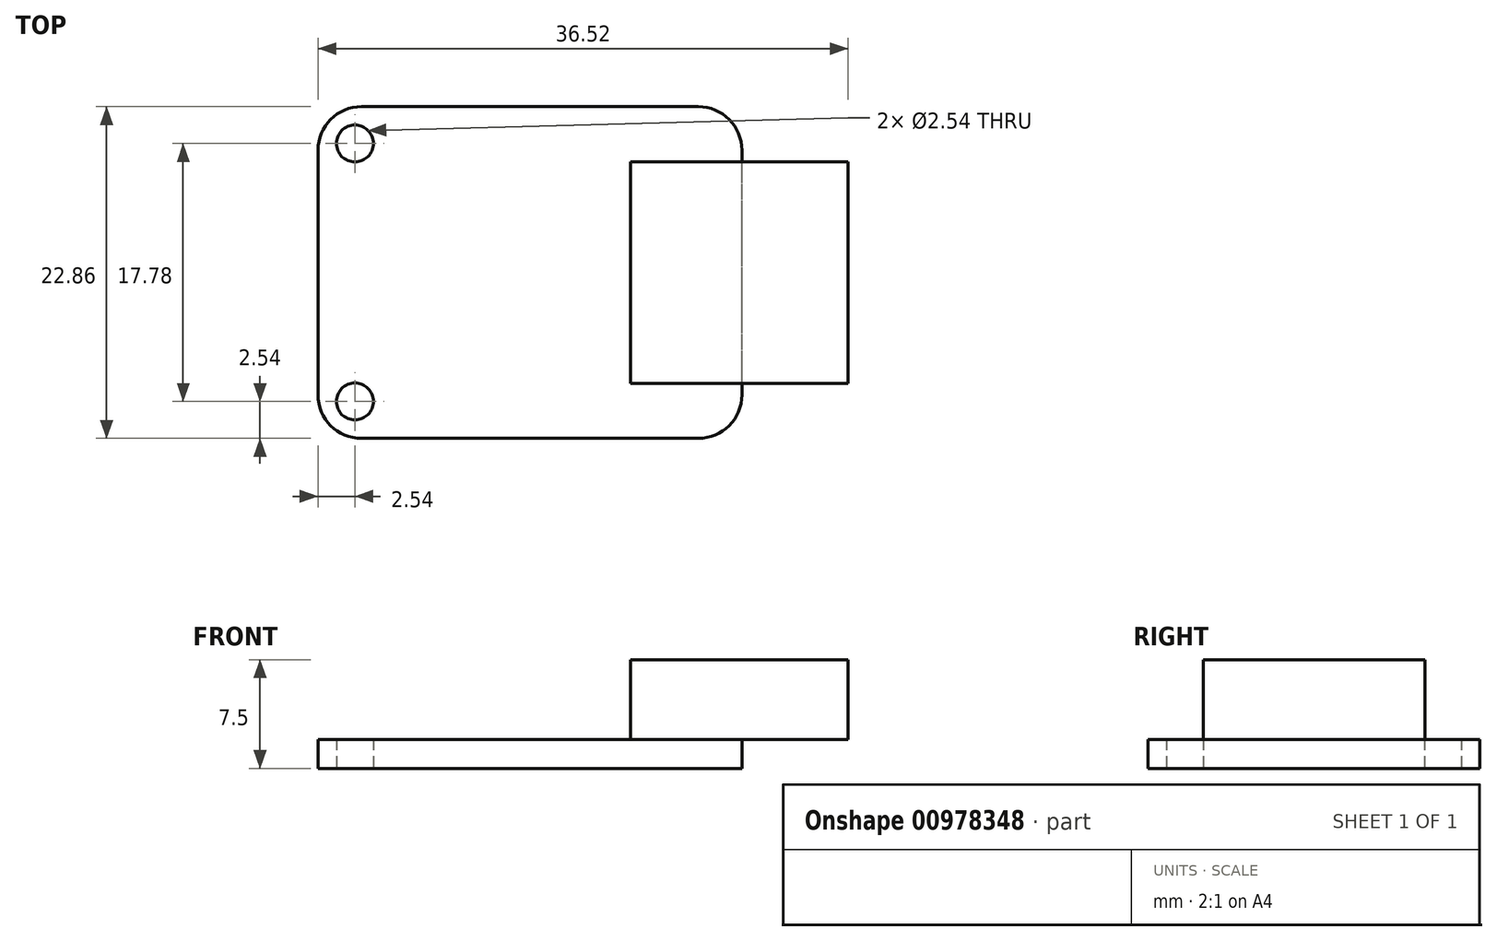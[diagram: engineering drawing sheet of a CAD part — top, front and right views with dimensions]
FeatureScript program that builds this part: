
annotation { "Feature Type Name" : "Feature", "Feature Type Description" : "" }
export const myFeature = defineFeature(function(context is Context, id is Id, definition is map)
    precondition{}
    {
        {
            var Q0;
            Q0=qCreatedBy(makeId("Top.planeOp"),FACE);
            var sketch = newSketch(context, id + "F0", { "sketchPlane" : qUnion([Q0])});
            skLineSegment(sketch, "E0.bottom", {"start": v(3, 0) * mm, "end": v(26.21, 0) * mm});
            skLineSegment(sketch, "E0.top", {"start": v(3, 22.86) * mm, "end": v(26.21, 22.86) * mm});
            skLineSegment(sketch, "E0.left", {"start": v(0, 3) * mm, "end": v(0, 19.86) * mm});
            skLineSegment(sketch, "E0.right", {"start": v(29.2, 3) * mm, "end": v(29.2, 19.86) * mm});
            skCircle(sketch, "E1", {"center": v(2.54, 2.54) * mm, "radius": 1.27 * mm});
            skCircle(sketch, "E2", {"center": v(2.54, 20.32) * mm, "radius": 1.27 * mm});
            skLineSegment(sketch, "E3", {"start": v(2.54, 2.54) * mm, "end": v(2.54, 0) * mm});
            skLineSegment(sketch, "E4", {"start": v(2.54, 2.54) * mm, "end": v(0, 2.54) * mm});
            skLineSegment(sketch, "E5", {"start": v(2.54, 20.32) * mm, "end": v(2.54, 22.86) * mm});
            skLineSegment(sketch, "E6", {"start": v(2.54, 20.32) * mm, "end": v(0, 20.32) * mm});
            skPoint(sketch, "E7.visualSharp", {"position": v(0, 22.86) * mm});
            skArc(sketch, "E7.filletArc", {"start": v(3, 22.86) * mm, "mid": v(0.88, 21.98) * mm, "end": v(0, 19.86) * mm});
            skPoint(sketch, "E8.visualSharp", {"position": v(0, 0) * mm});
            skArc(sketch, "E8.filletArc", {"start": v(0, 3) * mm, "mid": v(0.88, 0.88) * mm, "end": v(3, 0) * mm});
            skPoint(sketch, "E9.visualSharp", {"position": v(29.2, 22.86) * mm});
            skArc(sketch, "E9.filletArc", {"start": v(29.21, 19.86) * mm, "mid": v(28.33, 21.98) * mm, "end": v(26.21, 22.86) * mm});
            skPoint(sketch, "E10.visualSharp", {"position": v(29.2, 0) * mm});
            skArc(sketch, "E10.filletArc", {"start": v(26.21, 0) * mm, "mid": v(28.33, 0.88) * mm, "end": v(29.21, 3) * mm});
            skSolve(sketch);
        }
        {
            var Q0;
            {var subQ15=sQuery(id+"F0.wireOp",EDGE,"E0.bottom");Q0=makeQuery(id+"F0.imprint","IMPRINT",FACE,{"disambiguationData":[TD([[makeQuery(id+"F0.imprint","IMPRINT",EDGE,{"derivedFrom":subQ15}),1.0]])]});}
            var Q1;
            {var subQ0=sQuery(id+"F0.wireOp",EDGE,"E5");var subQ1=sQuery(id+"F0.wireOp",EDGE,"E2");var subQ2=makeQuery(id+"F0.imprint","INTERSECT",VERTEX,{"derivedFrom":[subQ1,subQ0]});Q1=makeQuery(id+"F0.imprint","IMPRINT",FACE,{"disambiguationData":[TD([[makeQuery(id+"F0.imprint","IMPRINT",EDGE,{"disambiguationData":[TD([[subQ2,-1.0]])],"derivedFrom":subQ1}),-1.0]])]});}
            var Q2;
            {var subQ0=sQuery(id+"F0.wireOp",EDGE,"E3");var subQ1=sQuery(id+"F0.wireOp",EDGE,"E1");var subQ2=makeQuery(id+"F0.imprint","INTERSECT",VERTEX,{"derivedFrom":[subQ1,subQ0]});Q2=makeQuery(id+"F0.imprint","IMPRINT",FACE,{"disambiguationData":[TD([[makeQuery(id+"F0.imprint","IMPRINT",EDGE,{"disambiguationData":[TD([[subQ2,1.0]])],"derivedFrom":subQ1}),-1.0]])]});}
            extrude(context, id + "F1", {"entities" : qUnion([Q0, Q1, Q2]), "depth" : 2 * mm, "offsetDistance" : 25 * mm});
        }
        {
            var Q0;
            Q0=makeQuery(id+"F1.opExtrude","CAP_FACE",FACE,{"disambiguationData":[OSD([sQuery(id+"F0.wireOp",EDGE,"E0.bottom"),sQuery(id+"F0.wireOp",EDGE,"E0.top"),sQuery(id+"F0.wireOp",EDGE,"E0.left"),sQuery(id+"F0.wireOp",EDGE,"E0.right"),sQuery(id+"F0.wireOp",EDGE,"E1"),sQuery(id+"F0.wireOp",EDGE,"E2"),sQuery(id+"F0.wireOp",EDGE,"E7.filletArc"),sQuery(id+"F0.wireOp",EDGE,"E8.filletArc"),sQuery(id+"F0.wireOp",EDGE,"E9.filletArc"),sQuery(id+"F0.wireOp",EDGE,"E10.filletArc")])],"isStart":false});
            var sketch = newSketch(context, id + "F2", { "sketchPlane" : qUnion([Q0])});
            skSolve(sketch);
        }
        {
            var Q0;
            Q0=makeQuery(id+"F2.imprint","IMPRINT",FACE,{"disambiguationData":[TD([[makeQuery(id+"F2.imprint","IMPRINT",EDGE,{"derivedFrom":makeQuery(id+"F1.opExtrude","CAP_EDGE",EDGE,{"disambiguationData":[OSD([sQuery(id+"F0.wireOp",EDGE,"E0.bottom")])],"isStart":false})}),1.0]])]});
            var sketch = newSketch(context, id + "F3", { "sketchPlane" : qUnion([Q0])});
            skLineSegment(sketch, "E11.bottom", {"start": v(21.52, 19.07) * mm, "end": v(36.52, 19.07) * mm});
            skLineSegment(sketch, "E11.top", {"start": v(21.52, 3.79) * mm, "end": v(36.52, 3.79) * mm});
            skLineSegment(sketch, "E11.left", {"start": v(21.52, 19.07) * mm, "end": v(21.52, 3.79) * mm});
            skLineSegment(sketch, "E11.right", {"start": v(36.52, 19.07) * mm, "end": v(36.52, 3.79) * mm});
            skLineSegment(sketch, "E12.0.0", {"start": v(26.21, 22.86) * mm, "end": v(3, 22.86) * mm});
            skArc(sketch, "E12.0.1", {"start": v(3, 22.86) * mm, "mid": v(0.88, 21.98) * mm, "end": v(0, 19.86) * mm});
            skLineSegment(sketch, "E12.0.2", {"start": v(0, 19.86) * mm, "end": v(0, 3) * mm});
            skArc(sketch, "E12.0.3", {"start": v(0, 3) * mm, "mid": v(0.88, 0.88) * mm, "end": v(3, 0) * mm});
            skLineSegment(sketch, "E12.0.4", {"start": v(3, 0) * mm, "end": v(26.21, 0) * mm});
            skArc(sketch, "E12.0.5", {"start": v(26.21, 0) * mm, "mid": v(28.33, 0.88) * mm, "end": v(29.21, 3) * mm});
            skLineSegment(sketch, "E12.0.6", {"start": v(29.2, 3) * mm, "end": v(29.2, 19.86) * mm});
            skArc(sketch, "E12.0.7", {"start": v(29.21, 19.86) * mm, "mid": v(28.33, 21.98) * mm, "end": v(26.21, 22.86) * mm});
            skLineSegment(sketch, "E13", {"start": v(21.52, 19.07) * mm, "end": v(21.52, 22.86) * mm});
            skLineSegment(sketch, "E14", {"start": v(21.52, 3.79) * mm, "end": v(21.52, 0) * mm});
            skSolve(sketch);
        }
        {
            var Q0;
            {var subQ0=sQuery(id+"F3.wireOp",EDGE,"E11.right");Q0=makeQuery(id+"F3.imprint","IMPRINT",FACE,{"disambiguationData":[TD([[makeQuery(id+"F3.imprint","IMPRINT",EDGE,{"derivedFrom":subQ0}),-1.0]])]});}
            var Q1;
            {var subQ0=sQuery(id+"F3.wireOp",EDGE,"E11.left");Q1=makeQuery(id+"F3.imprint","IMPRINT",FACE,{"disambiguationData":[TD([[makeQuery(id+"F3.imprint","IMPRINT",EDGE,{"derivedFrom":subQ0}),1.0]])]});}
            extrude(context, id + "F4", {"entities" : qUnion([Q0, Q1]), "operationType" : NewBodyOperationType.ADD, "depth" : 5.5 * mm, "offsetDistance" : 25 * mm});
        }
    });
